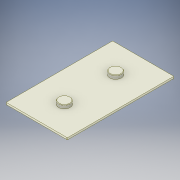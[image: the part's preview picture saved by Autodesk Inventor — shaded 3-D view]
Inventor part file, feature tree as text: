
AUTODESK INVENTOR PART (.ipt)
format: ipt  version: 2019.4 (Build 234330000, 330)  size: 163,328 bytes
history: native  units: in
note: dims shown in document units (in); Inventor stores cm internally (conversion verified against a paired STEP export)
features: extrude x3, fillet x3, sketch x3
ambient origin geometry x8: Origin, YZ Plane, XZ Plane, XY Plane, X Axis, Y Axis, Z Axis, Center Point
bodies: Solid1 (feature_tree)
feature tree (9):
  extrude  "Extrusion1"  Depth=1.0354in
  extrude  "Extrusion2"  Depth=0.0787in
  fillet  "Fillet1"  Radius=0.1969in
  fillet  "Fillet2"  Radius=0.4331in
  extrude  "Extrusion3"  Depth=0.0591in TaperAngle=0.0deg
  fillet  "Fillet3"  Radius=0.0079in
  sketch  "Sketch1"  dims[d0=1.7992in d1=1.0354in]
  sketch  "Sketch2"  dims[d2=0.0787in d3=0.0in d4=0.1969in d5=0.1969in d6=0.4331in]
  sketch  "Sketch3"  dims[d7=0.4331in d8=0.0591in d9=0.0in d10=0.0079in d11=0.0079in d12=0.7795in d13=1.5984in d14=0.0394in d15=0.0in d16=0.0079in]
